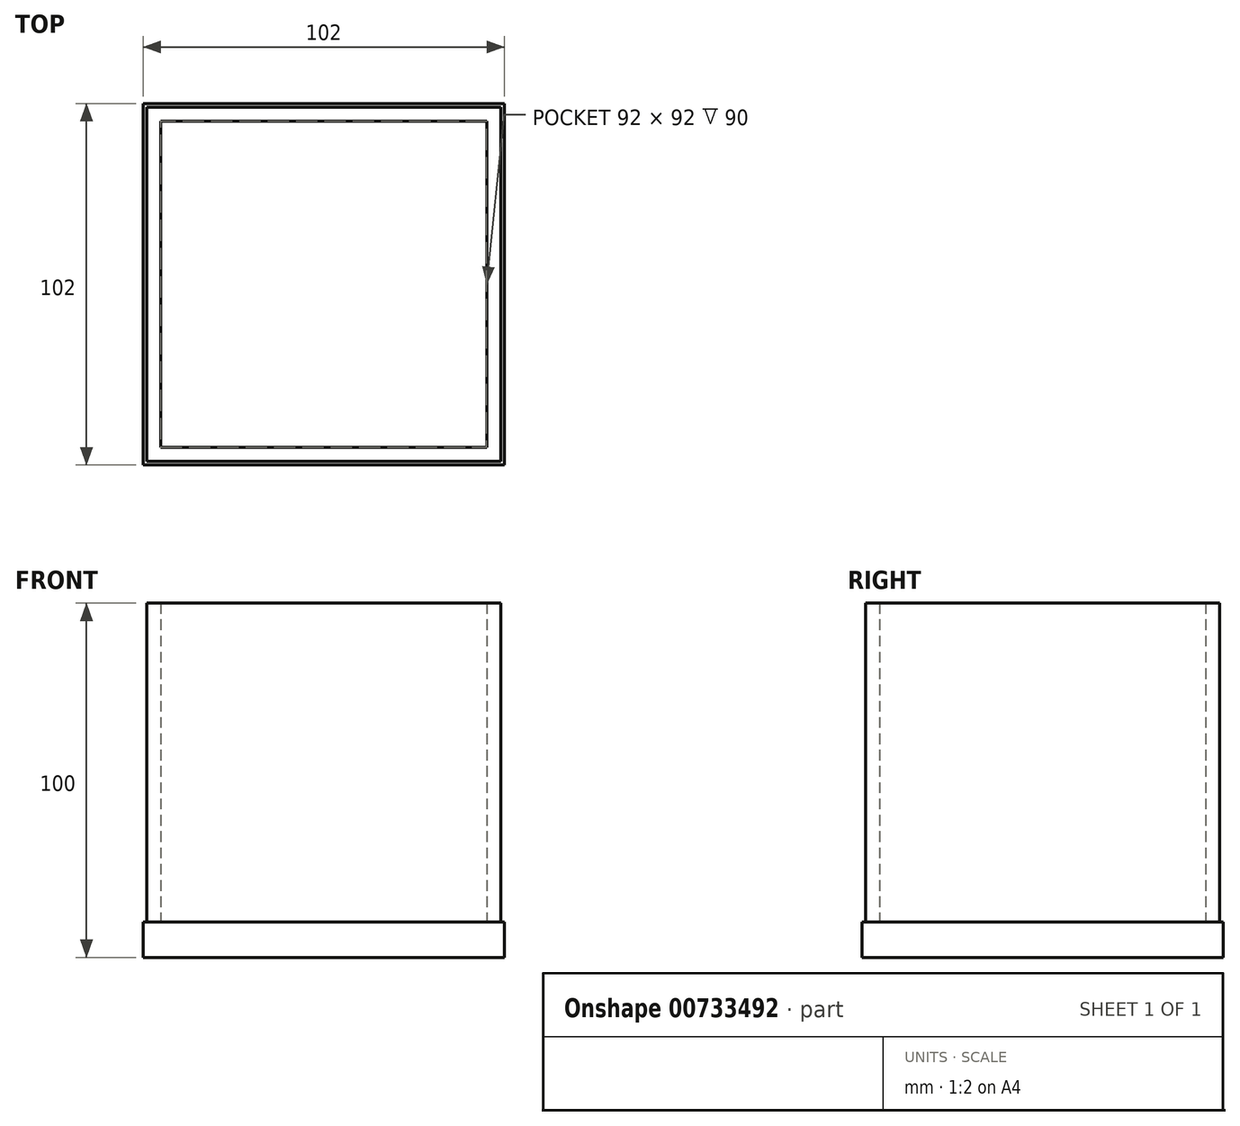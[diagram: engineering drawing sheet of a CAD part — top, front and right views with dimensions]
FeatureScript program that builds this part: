
annotation { "Feature Type Name" : "Feature", "Feature Type Description" : "" }
export const myFeature = defineFeature(function(context is Context, id is Id, definition is map)
    precondition{}
    {
        {
            var Q0;
            Q0=qCreatedBy(makeId("Top.planeOp"),FACE);
            var sketch = newSketch(context, id + "F0", { "sketchPlane" : qUnion([Q0])});
            skLineSegment(sketch, "E0.bottom", {"start": v(-50, 50) * mm, "end": v(50, 50) * mm});
            skLineSegment(sketch, "E0.top", {"start": v(-50, -50) * mm, "end": v(50, -50) * mm});
            skLineSegment(sketch, "E0.left", {"start": v(-50, 50) * mm, "end": v(-50, -50) * mm});
            skLineSegment(sketch, "E0.right", {"start": v(50, 50) * mm, "end": v(50, -50) * mm});
            skPoint(sketch, "E0.middle", {"position": v(0, 0) * mm});
            skLineSegment(sketch, "E1.bottom", {"start": v(-46, 46) * mm, "end": v(46, 46) * mm});
            skLineSegment(sketch, "E1.top", {"start": v(-46, -46) * mm, "end": v(46, -46) * mm});
            skLineSegment(sketch, "E1.left", {"start": v(-46, 46) * mm, "end": v(-46, -46) * mm});
            skLineSegment(sketch, "E1.right", {"start": v(46, 46) * mm, "end": v(46, -46) * mm});
            skSolve(sketch);
        }
        {
            var Q0;
            Q0=makeQuery(id+"F0.imprint","IMPRINT",FACE,{"disambiguationData":[TD([[makeQuery(id+"F0.imprint","IMPRINT",EDGE,{"derivedFrom":sQuery(id+"F0.wireOp",EDGE,"E0.bottom")}),-1.0]])]});
            extrude(context, id + "F1", {"entities" : qUnion([Q0]), "depth" : 90 * mm, "offsetDistance" : 25 * mm});
        }
        {
            var Q0;
            Q0=makeQuery(id+"F1.opExtrude","CAP_FACE",FACE,{"disambiguationData":[OSD([sQuery(id+"F0.wireOp",EDGE,"E0.bottom"),sQuery(id+"F0.wireOp",EDGE,"E0.top"),sQuery(id+"F0.wireOp",EDGE,"E0.left"),sQuery(id+"F0.wireOp",EDGE,"E0.right"),sQuery(id+"F0.wireOp",EDGE,"E1.bottom"),sQuery(id+"F0.wireOp",EDGE,"E1.top"),sQuery(id+"F0.wireOp",EDGE,"E1.left"),sQuery(id+"F0.wireOp",EDGE,"E1.right")])],"isStart":true});
            var sketch = newSketch(context, id + "F2", { "sketchPlane" : qUnion([Q0])});
            skLineSegment(sketch, "E2.bottom", {"start": v(51, 51) * mm, "end": v(-51, 51) * mm});
            skLineSegment(sketch, "E2.top", {"start": v(51, -51) * mm, "end": v(-51, -51) * mm});
            skLineSegment(sketch, "E2.left", {"start": v(51, 51) * mm, "end": v(51, -51) * mm});
            skLineSegment(sketch, "E2.right", {"start": v(-51, 51) * mm, "end": v(-51, -51) * mm});
            skPoint(sketch, "E2.middle", {"position": v(0, 0) * mm});
            skSolve(sketch);
        }
        {
            var Q0;
            Q0 = qSketchRegion(id + "F2", true);
            extrude(context, id + "F3", {"entities" : qUnion([Q0]), "operationType" : NewBodyOperationType.ADD, "depth" : 10 * mm, "offsetDistance" : 25 * mm});
        }
    });
